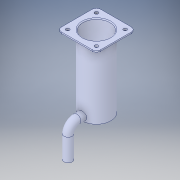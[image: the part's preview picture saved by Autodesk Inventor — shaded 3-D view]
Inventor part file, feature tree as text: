
AUTODESK INVENTOR PART (.ipt)
format: ipt  version: 2018 (Build 220112000, 112)  size: 199,680 bytes
history: native  units: in
note: dims shown in document units (in); Inventor stores cm internally (conversion verified against a paired STEP export)
features: extrude x1, sketch x1, projected_geometry x1, other x1
ambient origin geometry x8: Origin, YZ Plane, XZ Plane, XY Plane, X Axis, Y Axis, Z Axis, Center Point
bodies: Solid1 (feature_tree)
feature tree (4):
  extrude  "Extrusion1"  [1 undecoded]
  sketch  "Sketch1"  dims[d0=2.0in d1=0.0in]
  projected_geometry  "Projected Loop1"
  other  "Ø8.0mm Dowel Hole1"
note: 1 required parameter value undecoded (feature->parameter linkage not recoverable at this tier; creation-order binding heuristic only, values carry confidence <= 0.55)
